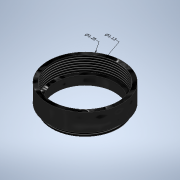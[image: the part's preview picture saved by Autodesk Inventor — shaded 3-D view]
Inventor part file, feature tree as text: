
AUTODESK INVENTOR PART (.ipt)
format: ipt  version: 2021.1 (Build 251245000, 245)  size: 141,312 bytes
history: native  units: in
note: dims shown in document units (in); Inventor stores cm internally (conversion verified against a paired STEP export)
features: other x3, sketch x3, thread x2, extrude x2, revolve x1
ambient origin geometry x8: Origin, YZ Plane, XZ Plane, XY Plane, X Axis, Y Axis, Z Axis, Center Point
bodies: Solid1 (feature_tree)
feature tree (11):
  other  "Annotations"
  revolve  "Revolution1"  [1 undecoded]
  thread  "Thread1"  [1 undecoded]
  extrude  "Extrusion1"  TaperAngle=90.0deg  [1 undecoded]
  extrude  "Extrusion2"  Depth=0.25in
  thread  "Thread2"  [1 undecoded]
  sketch  "Sketch1"  dims[d0=0.5625in d1=0.625in d2=0.1in]
  sketch  "Sketch3"  dims[d3=0.3in d4=90.0deg]
  sketch  "Sketch4"  dims[d5=0.1in d6=0.0in d7=1.125in d8=0.25in d9=0.0in d10=1.0in d11=0.25in d12=0.0in d13=0.25in d14=0.0in d15=2.248in d16=1.25in d17=2.1755in d18=1.125in]
  other  "Diameter Dimension 1"
  other  "Diameter Dimension 2"
note: 4 required parameter values undecoded (feature->parameter linkage not recoverable at this tier; creation-order binding heuristic only, values carry confidence <= 0.55)